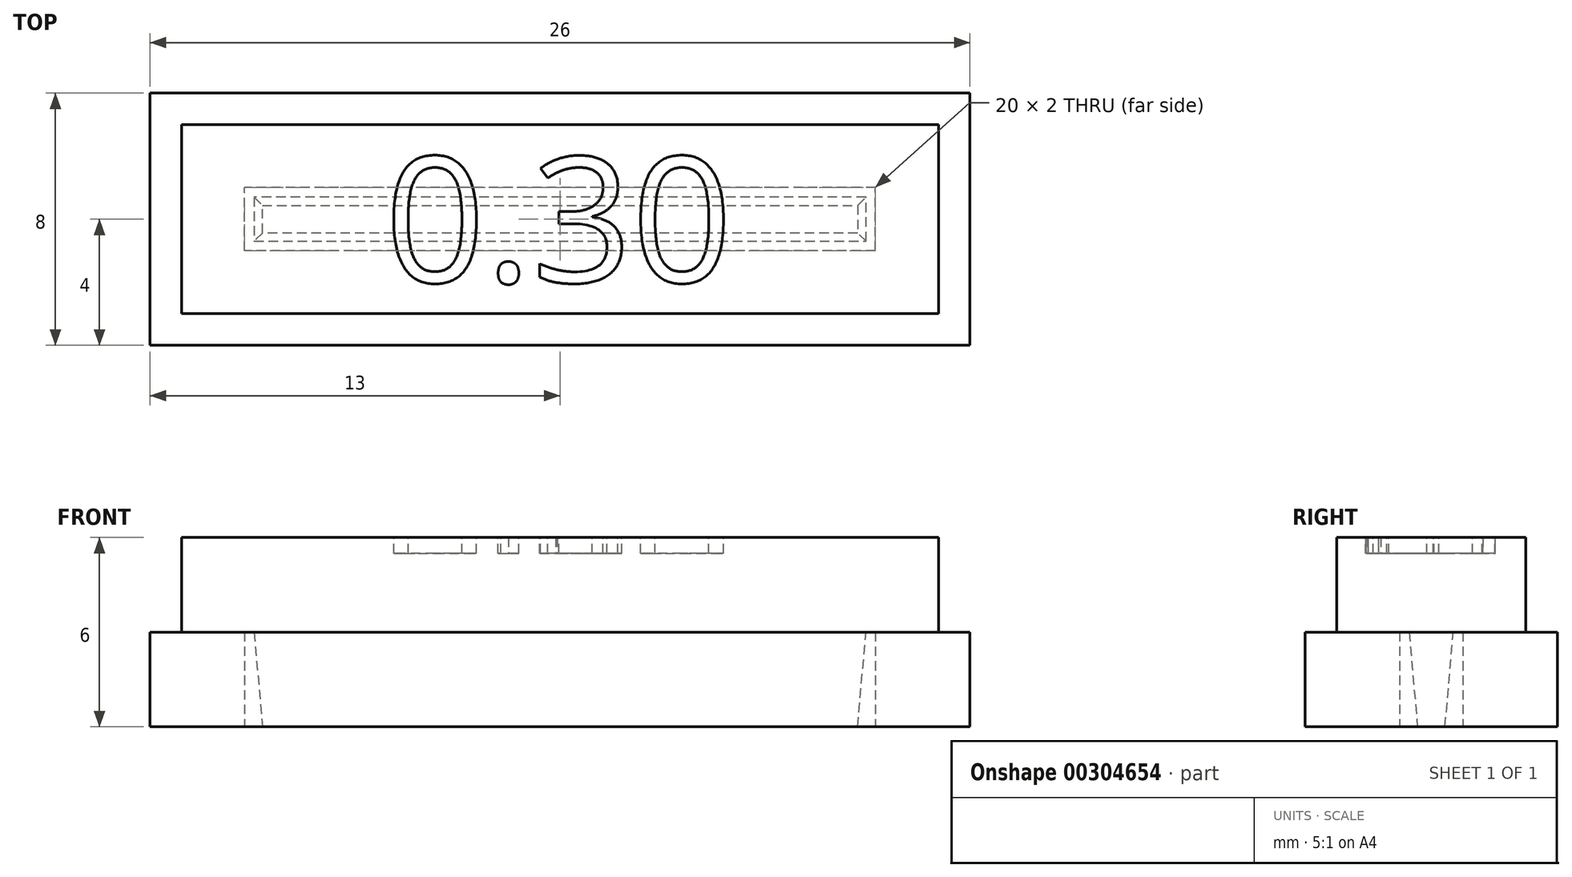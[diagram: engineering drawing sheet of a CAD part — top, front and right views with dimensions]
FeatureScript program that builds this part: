
annotation { "Feature Type Name" : "Feature", "Feature Type Description" : "" }
export const myFeature = defineFeature(function(context is Context, id is Id, definition is map)
    precondition{}
    {
        {
            var Q0;
            Q0=qCreatedBy(makeId("Top.planeOp"),FACE);
            var sketch = newSketch(context, id + "F0", { "sketchPlane" : qUnion([Q0])});
            skLineSegment(sketch, "E0.bottom", {"start": v(10, -1) * mm, "end": v(-10, -1) * mm});
            skLineSegment(sketch, "E0.top", {"start": v(10, 1) * mm, "end": v(-10, 1) * mm});
            skLineSegment(sketch, "E0.left", {"start": v(10, -1) * mm, "end": v(10, 1) * mm});
            skLineSegment(sketch, "E0.right", {"start": v(-10, -1) * mm, "end": v(-10, 1) * mm});
            skPoint(sketch, "E0.middle", {"position": v(0, 0) * mm});
            skLineSegment(sketch, "E1.0", {"start": v(13, 4) * mm, "end": v(-13, 4) * mm});
            skLineSegment(sketch, "E1.1", {"start": v(13, -4) * mm, "end": v(13, 4) * mm});
            skLineSegment(sketch, "E1.2", {"start": v(13, -4) * mm, "end": v(-13, -4) * mm});
            skLineSegment(sketch, "E1.3", {"start": v(-13, -4) * mm, "end": v(-13, 4) * mm});
            skSolve(sketch);
        }
        {
            var Q0;
            Q0=qSketchRegion(id+"F0",true);
            extrude(context, id + "F1", {"entities" : qUnion([Q0]), "depth" : 3 * mm});
        }
        {
            var Q0;
            Q0=makeQuery(id+"F1.opExtrude","CAP_FACE",FACE,{"disambiguationData":[OSD([sQuery(id+"F0.wireOp",EDGE,"E0.bottom"),sQuery(id+"F0.wireOp",EDGE,"E0.top"),sQuery(id+"F0.wireOp",EDGE,"E0.left"),sQuery(id+"F0.wireOp",EDGE,"E0.right"),sQuery(id+"F0.wireOp",EDGE,"E1.0"),sQuery(id+"F0.wireOp",EDGE,"E1.1"),sQuery(id+"F0.wireOp",EDGE,"E1.2"),sQuery(id+"F0.wireOp",EDGE,"E1.3")])],"isStart":false});
            var sketch = newSketch(context, id + "F2", { "sketchPlane" : qUnion([Q0])});
            skLineSegment(sketch, "E2.0", {"start": v(12, 3) * mm, "end": v(-12, 3) * mm});
            skLineSegment(sketch, "E2.1", {"start": v(12, -3) * mm, "end": v(12, 3) * mm});
            skLineSegment(sketch, "E2.2", {"start": v(12, -3) * mm, "end": v(-12, -3) * mm});
            skLineSegment(sketch, "E2.3", {"start": v(-12, -3) * mm, "end": v(-12, 3) * mm});
            skSolve(sketch);
        }
        {
            var Q0;
            Q0=qSketchRegion(id+"F2",true);
            extrude(context, id + "F3", {"entities" : qUnion([Q0]), "depth" : 3 * mm});
        }
        {
            var Q0;
            Q0=makeQuery(id+"F3.opExtrude","CAP_FACE",FACE,{"disambiguationData":[OSD([sQuery(id+"F2.wireOp",EDGE,"E2.0"),sQuery(id+"F2.wireOp",EDGE,"E2.1"),sQuery(id+"F2.wireOp",EDGE,"E2.2"),sQuery(id+"F2.wireOp",EDGE,"E2.3")])],"isStart":true});
            var sketch = newSketch(context, id + "F4", { "sketchPlane" : qUnion([Q0])});
            skLineSegment(sketch, "E3.0", {"start": v(-9.7, 0.7) * mm, "end": v(-9.7, -0.7) * mm});
            skLineSegment(sketch, "E3.1", {"start": v(9.7, 0.7) * mm, "end": v(-9.7, 0.7) * mm});
            skLineSegment(sketch, "E3.2", {"start": v(9.7, 0.7) * mm, "end": v(9.7, -0.7) * mm});
            skLineSegment(sketch, "E3.3", {"start": v(9.7, -0.7) * mm, "end": v(-9.7, -0.7) * mm});
            skSolve(sketch);
        }
        {
            var Q0;
            Q0=qSketchRegion(id+"F4",true);
            var Q1;
            Q1=makeQuery(id+"F1.opExtrude","CAP_FACE",FACE,{"disambiguationData":[OSD([sQuery(id+"F0.wireOp",EDGE,"E0.bottom"),sQuery(id+"F0.wireOp",EDGE,"E0.top"),sQuery(id+"F0.wireOp",EDGE,"E0.left"),sQuery(id+"F0.wireOp",EDGE,"E0.right"),sQuery(id+"F0.wireOp",EDGE,"E1.0"),sQuery(id+"F0.wireOp",EDGE,"E1.1"),sQuery(id+"F0.wireOp",EDGE,"E1.2"),sQuery(id+"F0.wireOp",EDGE,"E1.3")])],"isStart":true});
            extrude(context, id + "F5", {"entities" : qUnion([Q0]), "operationType" : NewBodyOperationType.ADD, "endBound" : BoundingType.UP_TO_SURFACE, "endBoundEntityFace" : qUnion([Q1]), "depth" : 25 * mm, "hasDraft" : true, "draftAngle" : 5 * degree, "draftPullDirection" : true});
        }
        {
            var Q0;
            Q0=makeQuery(id+"F3.opExtrude","CAP_FACE",FACE,{"disambiguationData":[OSD([sQuery(id+"F2.wireOp",EDGE,"E2.0"),sQuery(id+"F2.wireOp",EDGE,"E2.1"),sQuery(id+"F2.wireOp",EDGE,"E2.2"),sQuery(id+"F2.wireOp",EDGE,"E2.3")])],"isStart":false});
            var sketch = newSketch(context, id + "F6", { "sketchPlane" : qUnion([Q0])});
            skText(sketch, "E4", { "text": "0.30", "fontName": "OpenSans-Regular.ttf"});
            const initialGuessF6  = {"E4": [-0.00555, -0.002, 1, 0, 0.004]};
            skSetInitialGuess(sketch, initialGuessF6);
            skSolve(sketch);
        }
        {
            var Q0;
            Q0=qSketchRegion(id+"F6",true);
            extrude(context, id + "F7", {"entities" : qUnion([Q0]), "operationType" : NewBodyOperationType.REMOVE, "oppositeDirection" : true, "depth" : 0.5 * mm});
        }
    });
